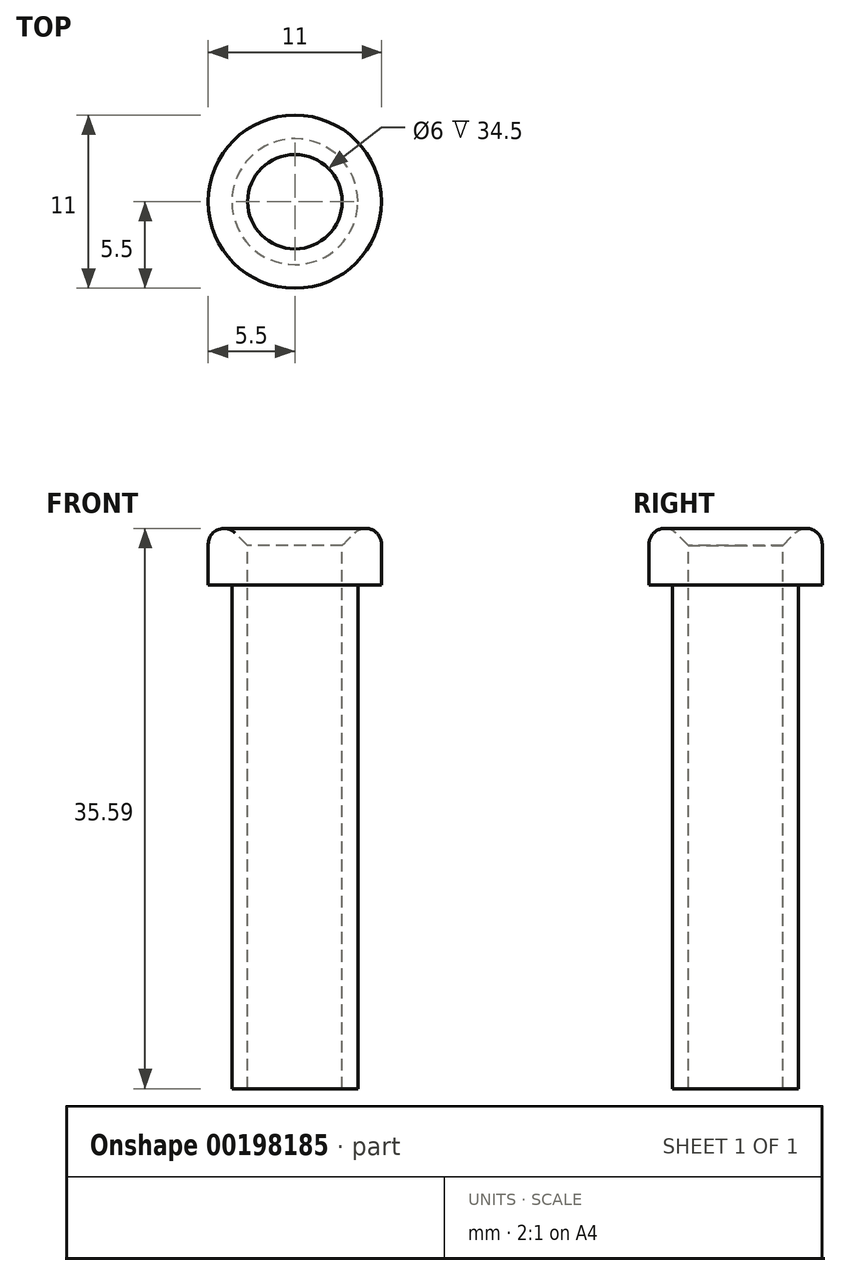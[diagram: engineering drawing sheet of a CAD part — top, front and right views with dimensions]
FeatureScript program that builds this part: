
annotation { "Feature Type Name" : "Feature", "Feature Type Description" : "" }
export const myFeature = defineFeature(function(context is Context, id is Id, definition is map)
    precondition{}
    {
        {
            var Q0;
            Q0=qCreatedBy(makeId("Top.planeOp"),FACE);
            var sketch = newSketch(context, id + "F0", { "sketchPlane" : qUnion([Q0])});
            skCircle(sketch, "E0", {"center": v(0, 0) * mm, "radius": 4 * mm});
            skCircle(sketch, "E1", {"center": v(0, 0) * mm, "radius": 3 * mm});
            skSolve(sketch);
        }
        {
            var Q0;
            Q0=makeQuery(id+"F0.imprint","IMPRINT",FACE,{"disambiguationData":[TD([[makeQuery(id+"F0.imprint","IMPRINT",EDGE,{"derivedFrom":sQuery(id+"F0.wireOp",EDGE,"E1")}),1.0]])]});
            var Q1;
            Q1=makeQuery(id+"F0.imprint","IMPRINT",FACE,{"disambiguationData":[TD([[makeQuery(id+"F0.imprint","IMPRINT",EDGE,{"derivedFrom":sQuery(id+"F0.wireOp",EDGE,"E0")}),1.0]])]});
            var Q2;
            Q2=sQuery(id+"F0.wireOp",EDGE,"E0");
            var Q3;
            Q3=sQuery(id+"F0.wireOp",EDGE,"E1");
            extrude(context, id + "F1", {"entities" : qUnion([Q0, Q1]), "surfaceEntities" : qUnion([Q2, Q3]), "depth" : 25 * mm});
        }
        {
            var Q0;
            Q0=makeQuery(id+"F1.opExtrude","CAP_FACE",FACE,{"disambiguationData":[OSD([sQuery(id+"F0.wireOp",EDGE,"E0")])],"isStart":false});
            var sketch = newSketch(context, id + "F2", { "sketchPlane" : qUnion([Q0])});
            skPoint(sketch, "E2", {"position": v(0, 0) * mm});
            skSolve(sketch);
        }
        {
            var Q0;
            Q0=makeQuery(id+"F2.imprint","IMPRINT",FACE,{"disambiguationData":[TD([[makeQuery(id+"F2.imprint","IMPRINT",EDGE,{"derivedFrom":makeQuery(id+"F1.opExtrude","CAP_EDGE",EDGE,{"disambiguationData":[OSD([sQuery(id+"F0.wireOp",EDGE,"E0")])],"isStart":false})}),1.0]])]});
            var sketch = newSketch(context, id + "F3", { "sketchPlane" : qUnion([Q0])});
            skCircle(sketch, "E3", {"center": v(0, 0) * mm, "radius": 5.5 * mm});
            skSolve(sketch);
        }
        {
            var Q0;
            Q0=makeQuery(id+"F3.imprint","IMPRINT",FACE,{"disambiguationData":[TD([[makeQuery(id+"F3.imprint","IMPRINT",EDGE,{"derivedFrom":sQuery(id+"F3.wireOp",EDGE,"E3")}),1.0]])]});
            var Q1;
            Q1=makeQuery(id+"F2.imprint","IMPRINT",FACE,{"disambiguationData":[TD([[makeQuery(id+"F2.imprint","IMPRINT",EDGE,{"derivedFrom":makeQuery(id+"F1.opExtrude","CAP_EDGE",EDGE,{"disambiguationData":[OSD([sQuery(id+"F0.wireOp",EDGE,"E0")])],"isStart":false})}),1.0]])]});
            extrude(context, id + "F4", {"entities" : qUnion([Q0, Q1]), "operationType" : NewBodyOperationType.ADD, "depth" : 5 * mm});
        }
        {
            var Q0;
            {var subQ0=sQuery(id+"F0.wireOp",EDGE,"E0");Q0=makeQuery(id+"F4.boolean.opBoolean","MERGE",FACE,{"derivedFrom":[makeQuery(id+"F4.opExtrude","CAP_FACE",FACE,{"disambiguationData":[OSD([subQ0])],"isStart":false}),makeQuery(id+"F4.opExtrude","CAP_FACE",FACE,{"disambiguationData":[OSD([subQ0,sQuery(id+"F3.wireOp",EDGE,"E3")])],"isStart":false})]});}
            var sketch = newSketch(context, id + "F5", { "sketchPlane" : qUnion([Q0])});
            skPoint(sketch, "E4", {"position": v(0, 0) * mm});
            skSolve(sketch);
        }
        {
            var Q0;
            Q0=sQuery(id+"F5.wireOp",VERTEX,"E4");
            var Q1;
            Q1=makeQuery(id+"F1.opExtrude","SWEPT_BODY",BODY,{"disambiguationData":[OSD([sQuery(id+"F0.wireOp",EDGE,"E0")])]});
            hole(context, id + "F6", {"style" : HoleStyle.C_SINK, "endStyle" : HoleEndStyle.THROUGH, "holeDiameter" : 6 * mm, "cSinkDiameter" : 11 * mm, "cSinkAngle" : 90 * degree, "locations" : qUnion([Q0]), "scope" : qUnion([Q1]), "isTappedThrough" : true});
        }
        {
            var Q0;
            Q0=makeQuery(id+"F6.hole-0.boolean.opBoolean","MERGE",EDGE,{"derivedFrom":[makeQuery(id+"F4.opExtrude","CAP_EDGE",EDGE,{"disambiguationData":[OSD([sQuery(id+"F3.wireOp",EDGE,"E3")])],"isStart":false}),makeQuery(id+"F6.hole-0.opRevolve","SWEPT_EDGE",EDGE,{"disambiguationData":[OSD([sQuery(id+"F6.hole-0.sketch.wireOp",EDGE,"csink_start_line_1"),sQuery(id+"F6.hole-0.sketch.wireOp",EDGE,"csink_start_line_2")])]})]});
            fillet(context, id + "F7", {"entities" : qUnion([Q0]), "radius" : 1 * mm, "tangentPropagation" : true, "allowEdgeOverflow" : false});
        }
        {
            var Q0;
            Q0=makeQuery(id+"F1.opExtrude","CAP_FACE",FACE,{"disambiguationData":[OSD([sQuery(id+"F0.wireOp",EDGE,"E0")])],"isStart":true});
            extrude(context, id + "F8", {"entities" : qUnion([Q0]), "operationType" : NewBodyOperationType.ADD, "depth" : 7 * mm});
        }
    });
